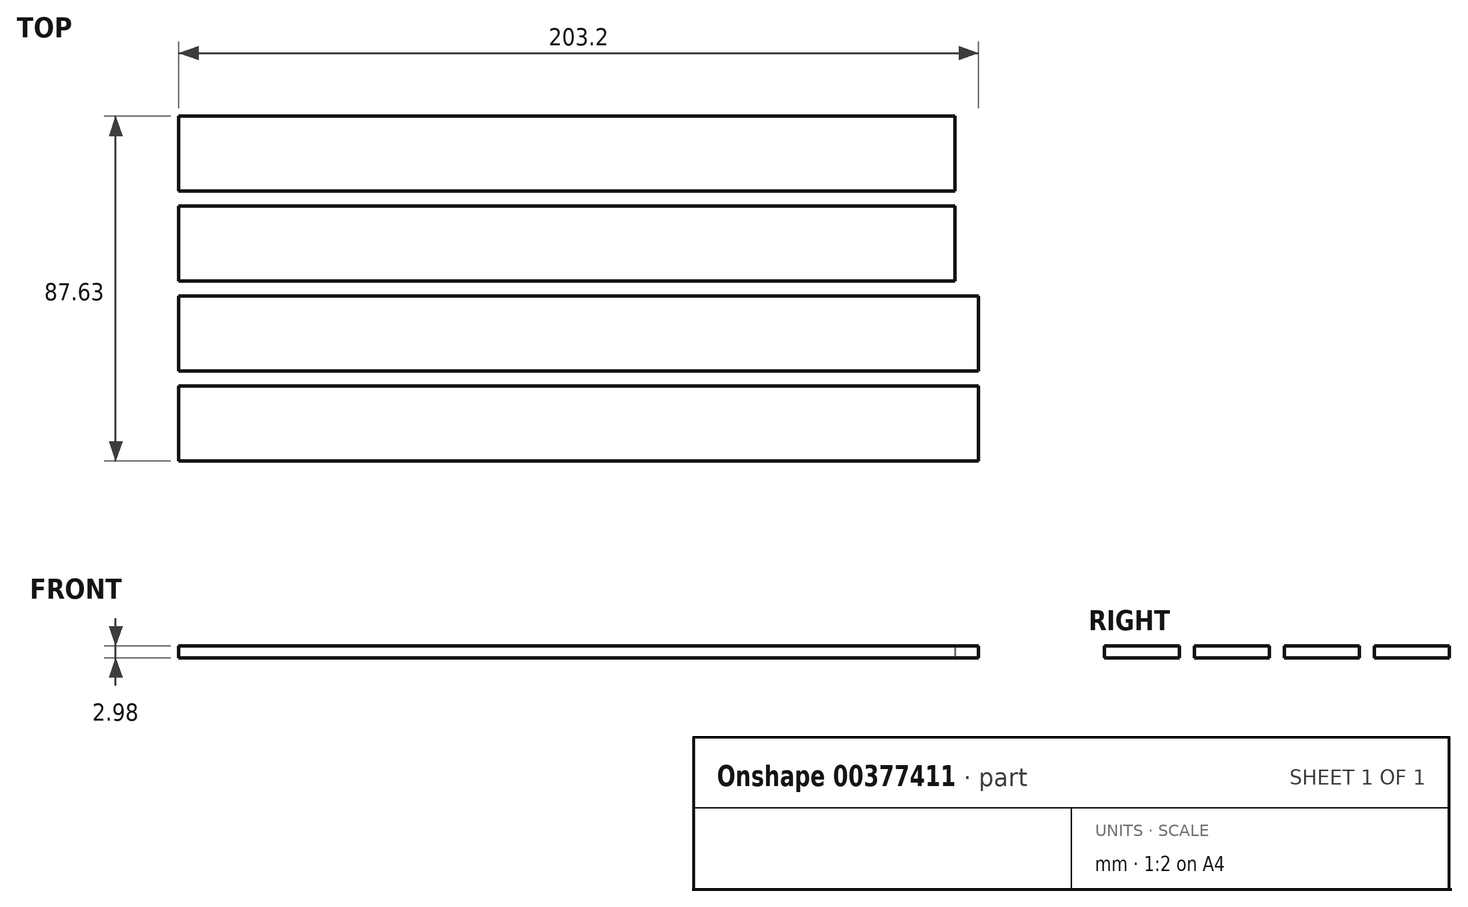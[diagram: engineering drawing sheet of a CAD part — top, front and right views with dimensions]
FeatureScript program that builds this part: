
annotation { "Feature Type Name" : "Feature", "Feature Type Description" : "" }
export const myFeature = defineFeature(function(context is Context, id is Id, definition is map)
    precondition{}
    {
        {
            var Q0;
            Q0=qCreatedBy(makeId("Top.planeOp"),FACE);
            var sketch = newSketch(context, id + "F0", { "sketchPlane" : qUnion([Q0])});
            skLineSegment(sketch, "E0.bottom", {"start": v(0, 0) * mm, "end": v(203.2, 0) * mm});
            skLineSegment(sketch, "E0.top", {"start": v(0, 19.05) * mm, "end": v(203.2, 19.05) * mm});
            skLineSegment(sketch, "E0.left", {"start": v(0, 0) * mm, "end": v(0, 19.05) * mm});
            skLineSegment(sketch, "E0.right", {"start": v(203.2, 0) * mm, "end": v(203.2, 19.05) * mm});
            skLineSegment(sketch, "E1.0.1.0", {"start": v(0, 22.86) * mm, "end": v(203.2, 22.86) * mm});
            skLineSegment(sketch, "E1.0.1.1", {"start": v(0, 41.91) * mm, "end": v(203.2, 41.91) * mm});
            skLineSegment(sketch, "E1.0.1.2", {"start": v(0, 22.86) * mm, "end": v(0, 41.91) * mm});
            skLineSegment(sketch, "E1.0.1.3", {"start": v(203.2, 22.86) * mm, "end": v(203.2, 41.91) * mm});
            skLineSegment(sketch, "E1.0.2.0", {"start": v(0, 45.72) * mm, "end": v(197.23, 45.72) * mm});
            skLineSegment(sketch, "E1.0.2.1", {"start": v(0, 64.77) * mm, "end": v(197.23, 64.77) * mm});
            skLineSegment(sketch, "E1.0.2.2", {"start": v(0, 45.72) * mm, "end": v(0, 64.77) * mm});
            skLineSegment(sketch, "E1.0.2.3", {"start": v(197.23, 45.72) * mm, "end": v(197.23, 64.77) * mm});
            skLineSegment(sketch, "E1.0.3.0", {"start": v(0, 68.58) * mm, "end": v(197.23, 68.58) * mm});
            skLineSegment(sketch, "E1.0.3.1", {"start": v(0, 87.63) * mm, "end": v(197.23, 87.63) * mm});
            skLineSegment(sketch, "E1.0.3.2", {"start": v(0, 68.58) * mm, "end": v(0, 87.63) * mm});
            skLineSegment(sketch, "E1.0.3.3", {"start": v(197.23, 68.58) * mm, "end": v(197.23, 87.63) * mm});
            skLineSegment(sketch, "E1.direction1", {"start": v(0, 0) * mm, "end": v(25.4, 0) * mm, "construction": true});
            skLineSegment(sketch, "E1.direction2", {"start": v(0, 0) * mm, "end": v(0, 22.86) * mm, "construction": true});
            skSolve(sketch);
        }
        {
            var Q0;
            Q0 = qSketchRegion(id + "F0", true);
            extrude(context, id + "F1", {"entities" : qUnion([Q0]), "depth" : 2.98 * mm});
        }
    });
